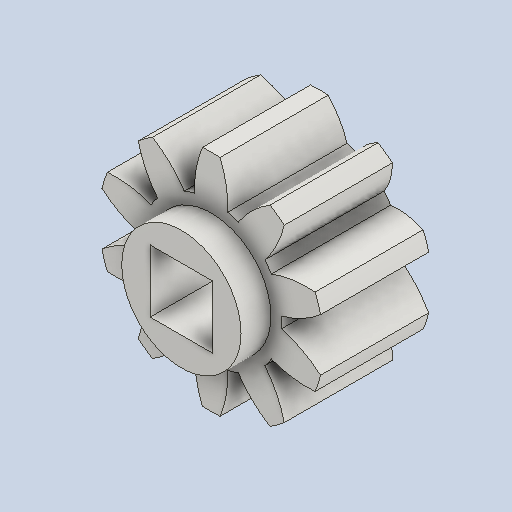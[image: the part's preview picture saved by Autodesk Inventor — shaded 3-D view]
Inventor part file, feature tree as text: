
AUTODESK INVENTOR PART (.ipt)
format: ipt  version: 2022 (Build 260153000, 153)  size: 284,160 bytes
history: native  units: in
note: dims shown in document units (in); Inventor stores cm internally (conversion verified against a paired STEP export)
features: other x12, sketch x6, plane x3
ambient origin geometry x8: Origin, YZ Plane, XZ Plane, XY Plane, X Axis, Y Axis, Z Axis, Center Point
bodies: Solid1 (feature_tree)
feature tree (21):
  other  "Spur Gear1"
  other  "Solid1::Spur Gear1"
  other  "TaggingFeature1"
  sketch  "Sketch1"  dims[d0=0.3937in]
  sketch  "Sketch2"  dims[d9=0.0in d14=0.0in d15=0.9352in d16=0.0in d17=0.0in d18=0.0in d19=0.9352in]
  sketch  "Sketch3"
  sketch  "Sketch4"
  sketch  "Sketch5"
  sketch  "Sketch6"
  plane  "XZ Plane_1"
  plane  "Work Plane2"
  plane  "Work Plane3"
  other  "Srf1"
  other  "Srf1::Derived"
  other  "Start plane iMate"
  other  "Distance iMate"
  other  "Position iMate"
  other  "Mesh iMate"
  other  "Axis iMate"
  other  "Mesh iMate2"
  other  "Align iMate"
